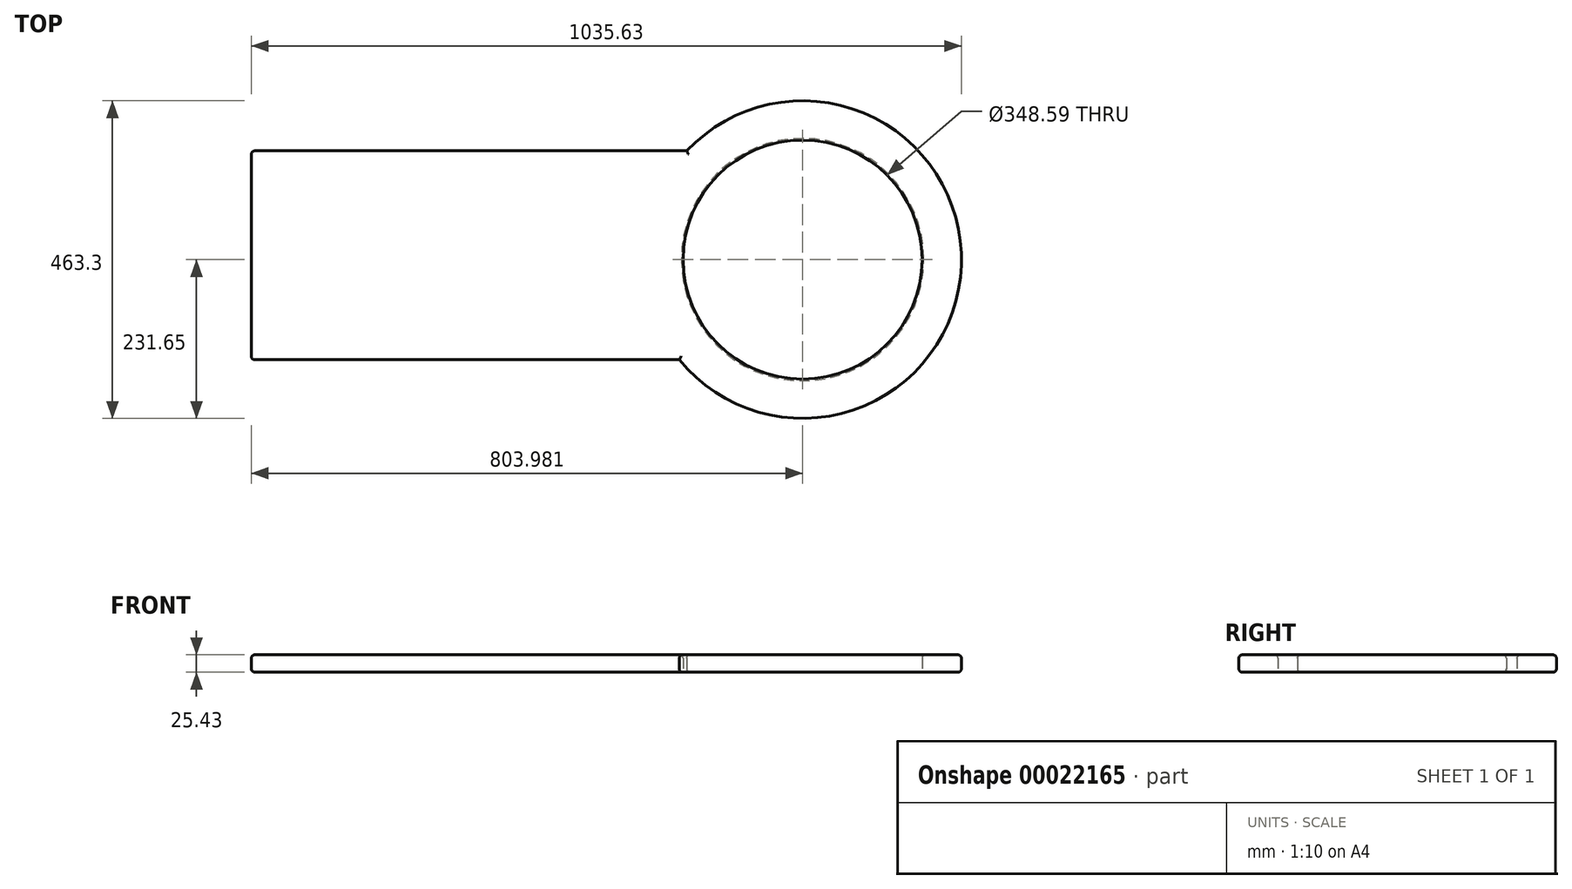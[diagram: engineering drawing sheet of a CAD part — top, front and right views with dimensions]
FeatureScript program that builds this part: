
annotation { "Feature Type Name" : "Feature", "Feature Type Description" : "" }
export const myFeature = defineFeature(function(context is Context, id is Id, definition is map)
    precondition{}
    {
        {
            var Q0;
            Q0=qCreatedBy(makeId("Top.planeOp"),FACE);
            var sketch = newSketch(context, id + "F0", { "sketchPlane" : qUnion([Q0])});
            skLineSegment(sketch, "E0.bottom", {"start": v(-349.26, 158.6) * mm, "end": v(348.93, 158.6) * mm});
            skLineSegment(sketch, "E0.top", {"start": v(-349.26, -146.2) * mm, "end": v(348.93, -146.2) * mm});
            skLineSegment(sketch, "E0.left", {"start": v(-349.26, 158.6) * mm, "end": v(-349.26, -146.2) * mm});
            skLineSegment(sketch, "E0.right", {"start": v(348.93, 158.6) * mm, "end": v(348.93, -146.2) * mm});
            skCircle(sketch, "E1", {"center": v(454.72, 0) * mm, "radius": 231.65 * mm});
            skCircle(sketch, "E2", {"center": v(454.72, 0) * mm, "radius": 174.3 * mm});
            skSolve(sketch);
        }
        {
            var Q0;
            Q0=makeQuery(id+"F0.imprint","IMPRINT",FACE,{"disambiguationData":[TD([[makeQuery(id+"F0.imprint","IMPRINT",EDGE,{"derivedFrom":sQuery(id+"F0.wireOp",EDGE,"E0.bottom")}),-1.0]])]});
            extrude(context, id + "F1", {"entities" : qUnion([Q0]), "depth" : 25.4 * mm});
        }
        {
            var Q0;
            Q0=makeQuery(id+"F1.opExtrude","CAP_EDGE",EDGE,{"disambiguationData":[OSD([sQuery(id+"F0.wireOp",EDGE,"E0.bottom")])],"isStart":false});
            var Q1;
            Q1=makeQuery(id+"F1.opExtrude","CAP_EDGE",EDGE,{"disambiguationData":[OSD([sQuery(id+"F0.wireOp",EDGE,"E0.left")])],"isStart":false});
            chamfer(context, id + "F2", {"entities" : qUnion([Q0, Q1]), "width" : 5.08 * mm, "tangentPropagation" : true});
        }
        {
            var Q0;
            Q0=makeQuery(id+"F1.opExtrude","CAP_EDGE",EDGE,{"disambiguationData":[OSD([sQuery(id+"F0.wireOp",EDGE,"E0.top")])],"isStart":false});
            var Q1;
            Q1=makeQuery(id+"F1.opExtrude","CAP_EDGE",EDGE,{"disambiguationData":[OSD([sQuery(id+"F0.wireOp",EDGE,"E0.right")])],"isStart":false});
            chamfer(context, id + "F3", {"entities" : qUnion([Q0, Q1]), "width" : 5.08 * mm, "tangentPropagation" : true});
        }
        {
            var Q0;
            Q0=makeQuery(id+"F1.opExtrude","SWEPT_EDGE",EDGE,{"disambiguationData":[OSD([sQuery(id+"F0.wireOp",EDGE,"E0.top"),sQuery(id+"F0.wireOp",EDGE,"E0.left")])]});
            var Q1;
            Q1=makeQuery(id+"F1.opExtrude","CAP_EDGE",EDGE,{"disambiguationData":[OSD([sQuery(id+"F0.wireOp",EDGE,"E0.top")])],"isStart":true});
            var Q2;
            Q2=makeQuery(id+"F1.opExtrude","CAP_EDGE",EDGE,{"disambiguationData":[OSD([sQuery(id+"F0.wireOp",EDGE,"E0.left")])],"isStart":true});
            chamfer(context, id + "F4", {"entities" : qUnion([Q0, Q1, Q2]), "width" : 5.08 * mm, "tangentPropagation" : true});
        }
        {
            var Q0;
            Q0=makeQuery(id+"F1.opExtrude","SWEPT_EDGE",EDGE,{"disambiguationData":[OSD([sQuery(id+"F0.wireOp",EDGE,"E0.bottom"),sQuery(id+"F0.wireOp",EDGE,"E0.left")])]});
            var Q1;
            Q1=makeQuery(id+"F1.opExtrude","CAP_EDGE",EDGE,{"disambiguationData":[OSD([sQuery(id+"F0.wireOp",EDGE,"E0.bottom")])],"isStart":true});
            chamfer(context, id + "F5", {"entities" : qUnion([Q0, Q1]), "width" : 5.08 * mm, "tangentPropagation" : true});
        }
        {
            var Q0;
            Q0=makeQuery(id+"F1.opExtrude","SWEPT_EDGE",EDGE,{"disambiguationData":[OSD([sQuery(id+"F0.wireOp",EDGE,"E0.bottom"),sQuery(id+"F0.wireOp",EDGE,"E0.right")])]});
            var Q1;
            Q1=makeQuery(id+"F1.opExtrude","CAP_EDGE",EDGE,{"disambiguationData":[OSD([sQuery(id+"F0.wireOp",EDGE,"E0.right")])],"isStart":true});
            chamfer(context, id + "F6", {"entities" : qUnion([Q0, Q1]), "width" : 5.08 * mm, "tangentPropagation" : true});
        }
        {
            var Q0;
            Q0 = qSketchRegion(id + "F0", true);
            extrude(context, id + "F7", {"entities" : qUnion([Q0]), "operationType" : NewBodyOperationType.ADD, "depth" : 25.4 * mm});
        }
        {
            var Q0;
            {var subQ0=sQuery(id+"F0.wireOp",EDGE,"E1");var subQ1=sQuery(id+"F0.wireOp",EDGE,"E0.left");var subQ2=sQuery(id+"F0.wireOp",EDGE,"E0.top");var subQ3=sQuery(id+"F0.wireOp",EDGE,"E0.bottom");Q0=makeQuery(id+"F7.boolean.opBoolean","MERGE",FACE,{"derivedFrom":[makeQuery(id+"F1.opExtrude","CAP_FACE",FACE,{"disambiguationData":[OSD([subQ3,subQ2,subQ1,subQ0])],"isStart":true}),makeQuery(id+"F7.opExtrude","CAP_FACE",FACE,{"disambiguationData":[OSD([subQ3,subQ2,subQ1,subQ0,sQuery(id+"F0.wireOp",EDGE,"E2")])],"isStart":true})]});}
            var sketch = newSketch(context, id + "F8", { "sketchPlane" : qUnion([Q0])});
            skCircle(sketch, "E3", {"center": v(454.72, 0) * mm, "radius": 176.75 * mm});
            skSolve(sketch);
        }
        {
            var Q0;
            Q0 = qSketchRegion(id + "F8", true);
            extrude(context, id + "F9", {"entities" : qUnion([Q0]), "depth" : 0.03 * mm});
        }
        {
            var Q0;
            Q0=makeQuery(id+"F7.opExtrude","CAP_EDGE",EDGE,{"disambiguationData":[OSD([sQuery(id+"F0.wireOp",EDGE,"E0.top")])],"isStart":false});
            fillet(context, id + "F10", {"entities" : qUnion([Q0]), "radius" : 5.08 * mm, "tangentPropagation" : true, "allowEdgeOverflow" : false});
        }
        {
            var Q0;
            Q0=makeQuery(id+"F7.opExtrude","CAP_EDGE",EDGE,{"disambiguationData":[OSD([sQuery(id+"F0.wireOp",EDGE,"E0.top")])],"isStart":true});
            fillet(context, id + "F11", {"entities" : qUnion([Q0]), "radius" : 5.08 * mm, "tangentPropagation" : true, "allowEdgeOverflow" : false});
        }
        {
            var Q0;
            Q0=makeQuery(id+"F7.opExtrude","SWEPT_EDGE",EDGE,{"disambiguationData":[OSD([sQuery(id+"F0.wireOp",EDGE,"E0.top"),sQuery(id+"F0.wireOp",EDGE,"E0.left")])]});
            fillet(context, id + "F12", {"entities" : qUnion([Q0]), "radius" : 5.08 * mm, "tangentPropagation" : true, "allowEdgeOverflow" : false});
        }
        {
            var Q0;
            Q0=makeQuery(id+"F7.opExtrude","CAP_EDGE",EDGE,{"disambiguationData":[OSD([sQuery(id+"F0.wireOp",EDGE,"E1")])],"isStart":false});
            fillet(context, id + "F13", {"entities" : qUnion([Q0]), "radius" : 5.08 * mm, "tangentPropagation" : true, "allowEdgeOverflow" : false});
        }
        {
            var Q0;
            Q0=makeQuery(id+"F7.opExtrude","CAP_EDGE",EDGE,{"disambiguationData":[OSD([sQuery(id+"F0.wireOp",EDGE,"E1")])],"isStart":true});
            fillet(context, id + "F14", {"entities" : qUnion([Q0]), "radius" : 5.08 * mm, "tangentPropagation" : true, "allowEdgeOverflow" : false});
        }
        {
            var Q0;
            Q0=makeQuery(id+"F7.opExtrude","CAP_EDGE",EDGE,{"disambiguationData":[OSD([sQuery(id+"F0.wireOp",EDGE,"E0.bottom")])],"isStart":false});
            fillet(context, id + "F15", {"entities" : qUnion([Q0]), "radius" : 5.08 * mm, "tangentPropagation" : true, "allowEdgeOverflow" : false});
        }
        {
            var Q0;
            Q0=makeQuery(id+"F7.opExtrude","CAP_EDGE",EDGE,{"disambiguationData":[OSD([sQuery(id+"F0.wireOp",EDGE,"E2")])],"isStart":false});
            fillet(context, id + "F16", {"entities" : qUnion([Q0]), "radius" : 5.08 * mm, "tangentPropagation" : true, "allowEdgeOverflow" : false});
        }
    });
